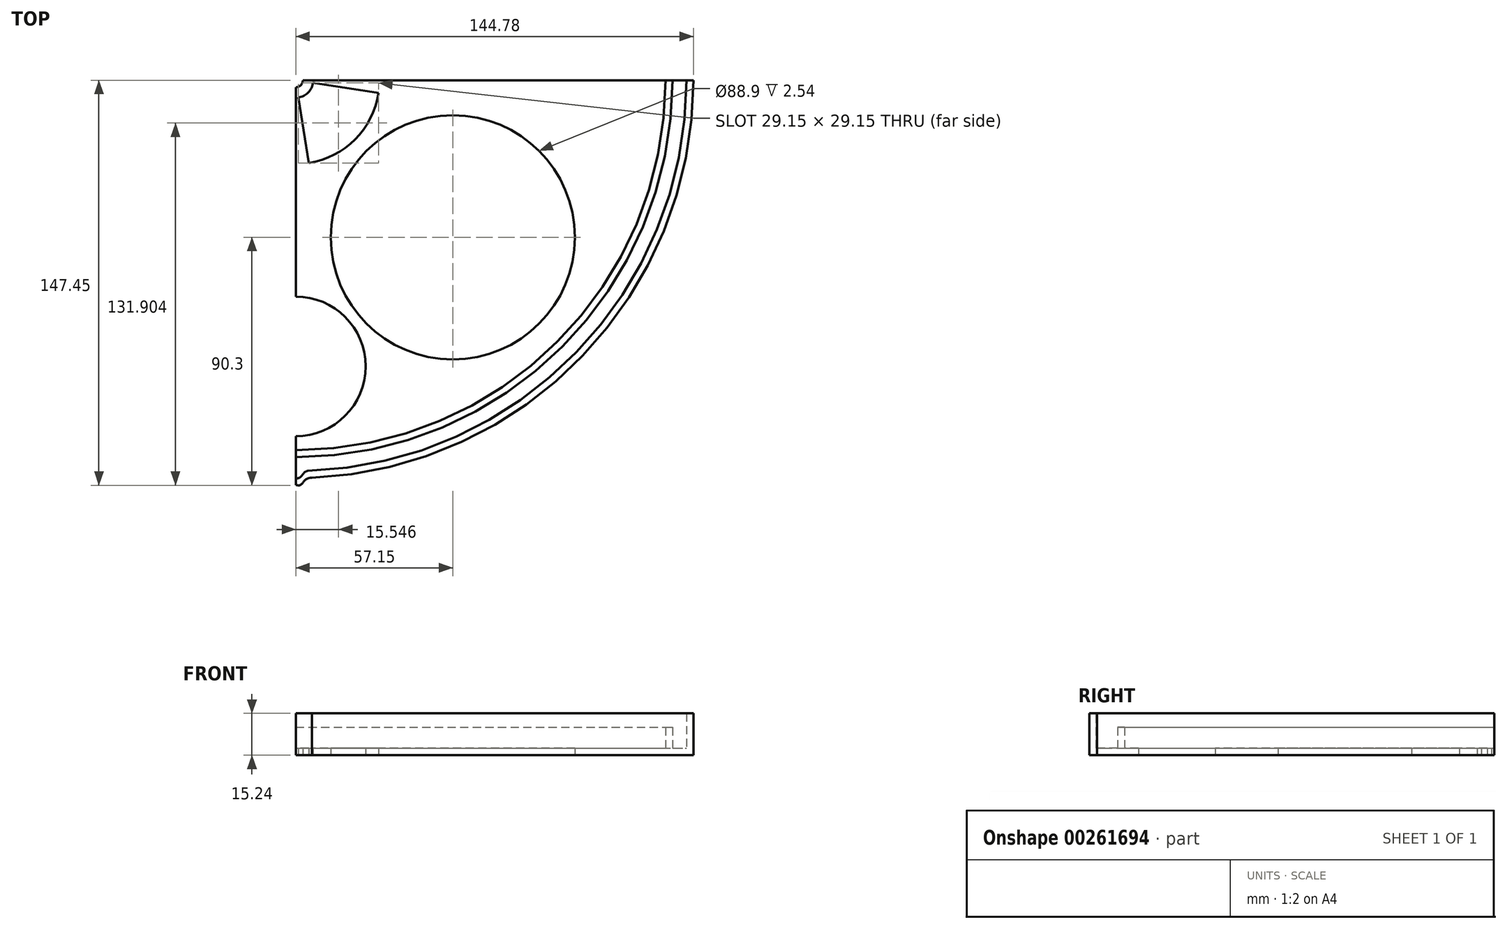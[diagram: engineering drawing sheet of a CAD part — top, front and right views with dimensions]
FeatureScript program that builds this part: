
annotation { "Feature Type Name" : "Feature", "Feature Type Description" : "" }
export const myFeature = defineFeature(function(context is Context, id is Id, definition is map)
    precondition{}
    {
        {
            var Q0;
            Q0=qCreatedBy(makeId("Top.planeOp"),FACE);
            var sketch = newSketch(context, id + "F0", { "sketchPlane" : qUnion([Q0])});
            skCircle(sketch, "E0", {"center": v(0, 0) * mm, "radius": 134.62 * mm});
            skCircle(sketch, "E1.0", {"center": v(0, 0) * mm, "radius": 137.16 * mm});
            skCircle(sketch, "E2.0", {"center": v(0, 0) * mm, "radius": 144.78 * mm});
            skCircle(sketch, "E3.0", {"center": v(0, 0) * mm, "radius": 142.24 * mm});
            skCircle(sketch, "E4.0", {"center": v(0, 0) * mm, "radius": 2.54 * mm});
            skLineSegment(sketch, "E5", {"start": v(0, 0) * mm, "end": v(0, -147.32) * mm});
            skLineSegment(sketch, "E6", {"start": v(-11.57, -144.32) * mm, "end": v(0, -147.32) * mm});
            skFitSpline(sketch, "E7", {"points": [v(0, -147.32) * mm, v(5.92, -144.66) * mm], "startDerivative": vector(10.02, -2.47) * mm, "endDerivative": vector(12.8, 0.33) * mm});
            skLineSegment(sketch, "E8", {"start": v(-8.6, -141.98) * mm, "end": v(0, -144.78) * mm});
            skFitSpline(sketch, "E9", {"points": [v(0, -144.78) * mm, v(4.46, -142.17) * mm], "startDerivative": vector(6.28, -2.02) * mm, "endDerivative": vector(5.88, 0.14) * mm});
            skLineSegment(sketch, "E10", {"start": v(0, 0) * mm, "end": v(-144.78, 0) * mm});
            skLineSegment(sketch, "E11", {"start": v(0, 0) * mm, "end": v(0, 144.78) * mm});
            skLineSegment(sketch, "E12", {"start": v(0, 0) * mm, "end": v(144.78, 0) * mm});
            skLineSegment(sketch, "E13", {"start": v(0, -12.7) * mm, "end": v(-144.22, -12.7) * mm});
            skLineSegment(sketch, "E14", {"start": v(0, -12.7) * mm, "end": v(144.78, -12.7) * mm});
            skLineSegment(sketch, "E15", {"start": v(0, 12.7) * mm, "end": v(-144.22, 12.7) * mm});
            skLineSegment(sketch, "E16", {"start": v(0, 12.7) * mm, "end": v(144.78, 12.7) * mm});
            skLineSegment(sketch, "E17", {"start": v(-12.7, 0) * mm, "end": v(-12.7, 144.22) * mm});
            skLineSegment(sketch, "E18", {"start": v(12.7, 0) * mm, "end": v(12.7, 144.22) * mm});
            skLineSegment(sketch, "E19", {"start": v(-12.7, 0) * mm, "end": v(-12.7, -144.22) * mm});
            skLineSegment(sketch, "E20", {"start": v(12.7, 0) * mm, "end": v(12.7, -144.22) * mm});
            skCircle(sketch, "E21", {"center": v(-57.15, -57.15) * mm, "radius": 44.45 * mm});
            skCircle(sketch, "E22", {"center": v(57.15, -57.15) * mm, "radius": 44.45 * mm});
            skCircle(sketch, "E23", {"center": v(-57.15, 57.15) * mm, "radius": 44.45 * mm});
            skCircle(sketch, "E24", {"center": v(57.15, 57.15) * mm, "radius": 44.45 * mm});
            skCircle(sketch, "E25", {"center": v(-104.14, 0) * mm, "radius": 25.4 * mm});
            skCircle(sketch, "E26", {"center": v(0, 104.14) * mm, "radius": 25.4 * mm});
            skCircle(sketch, "E27", {"center": v(104.14, 0) * mm, "radius": 25.4 * mm});
            skCircle(sketch, "E28", {"center": v(0, -104.14) * mm, "radius": 25.4 * mm});
            skCircle(sketch, "E29", {"center": v(0, 0) * mm, "radius": 30.48 * mm});
            skLineSegment(sketch, "E30", {"start": v(-12.7, -82.14) * mm, "end": v(0, 0) * mm});
            skLineSegment(sketch, "E31", {"start": v(12.7, -82.14) * mm, "end": v(0, 0) * mm});
            skLineSegment(sketch, "E32", {"start": v(82.14, -12.7) * mm, "end": v(0, 0) * mm});
            skLineSegment(sketch, "E33", {"start": v(82.14, 12.7) * mm, "end": v(0, 0) * mm});
            skLineSegment(sketch, "E34", {"start": v(12.7, 82.14) * mm, "end": v(0, 0) * mm});
            skLineSegment(sketch, "E35", {"start": v(-12.7, 82.14) * mm, "end": v(0, 0) * mm});
            skLineSegment(sketch, "E36", {"start": v(-82.14, -12.7) * mm, "end": v(0, 0) * mm});
            skLineSegment(sketch, "E37", {"start": v(-82.14, 12.7) * mm, "end": v(0, 0) * mm});
            skCircle(sketch, "E38", {"center": v(0, 0) * mm, "radius": 6.35 * mm});
            skSolve(sketch);
        }
        {
            var Q0;
            {var subQ1=sQuery(id+"F0.wireOp",EDGE,"E0");var subQ7=sQuery(id+"F0.wireOp",EDGE,"E20");var subQ12=makeQuery(id+"F0.imprint","INTERSECT",VERTEX,{"derivedFrom":[subQ1,subQ7]});Q0=makeQuery(id+"F0.imprint","IMPRINT",FACE,{"disambiguationData":[TD([[makeQuery(id+"F0.imprint","IMPRINT",EDGE,{"disambiguationData":[TD([[subQ12,-1.0]])],"derivedFrom":subQ1}),1.0]])]});}
            var Q1;
            {var subQ0=sQuery(id+"F0.wireOp",EDGE,"E5");var subQ1=sQuery(id+"F0.wireOp",EDGE,"E0");var subQ2=makeQuery(id+"F0.imprint","INTERSECT",VERTEX,{"derivedFrom":[subQ1,subQ0]});Q1=makeQuery(id+"F0.imprint","IMPRINT",FACE,{"disambiguationData":[TD([[makeQuery(id+"F0.imprint","IMPRINT",EDGE,{"disambiguationData":[TD([[subQ2,-1.0]])],"derivedFrom":subQ1}),1.0]])]});}
            var Q2;
            {var subQ0=sQuery(id+"F0.wireOp",EDGE,"E29");var subQ1=sQuery(id+"F0.wireOp",EDGE,"E5");var subQ2=makeQuery(id+"F0.imprint","INTERSECT",VERTEX,{"derivedFrom":[subQ1,subQ0]});Q2=makeQuery(id+"F0.imprint","IMPRINT",FACE,{"disambiguationData":[TD([[makeQuery(id+"F0.imprint","IMPRINT",EDGE,{"disambiguationData":[TD([[subQ2,-1.0]])],"derivedFrom":subQ1}),1.0]])]});}
            var Q3;
            {var subQ0=sQuery(id+"F0.wireOp",EDGE,"E29");var subQ1=sQuery(id+"F0.wireOp",EDGE,"E20");var subQ2=makeQuery(id+"F0.imprint","INTERSECT",VERTEX,{"derivedFrom":[subQ1,subQ0]});Q3=makeQuery(id+"F0.imprint","IMPRINT",FACE,{"disambiguationData":[TD([[makeQuery(id+"F0.imprint","IMPRINT",EDGE,{"disambiguationData":[TD([[subQ2,-1.0]])],"derivedFrom":subQ1}),-1.0]])]});}
            var Q4;
            {var subQ1=sQuery(id+"F0.wireOp",EDGE,"E5");var subQ3=sQuery(id+"F0.wireOp",EDGE,"E29");var subQ4=makeQuery(id+"F0.imprint","INTERSECT",VERTEX,{"derivedFrom":[subQ1,subQ3]});Q4=makeQuery(id+"F0.imprint","IMPRINT",FACE,{"disambiguationData":[TD([[makeQuery(id+"F0.imprint","IMPRINT",EDGE,{"disambiguationData":[TD([[subQ4,-1.0]])],"derivedFrom":subQ3}),1.0]])]});}
            var Q5;
            {var subQ0=sQuery(id+"F0.wireOp",EDGE,"E14");var subQ5=sQuery(id+"F0.wireOp",EDGE,"E31");var subQ6=makeQuery(id+"F0.imprint","INTERSECT",VERTEX,{"derivedFrom":[subQ0,subQ5]});Q5=makeQuery(id+"F0.imprint","IMPRINT",FACE,{"disambiguationData":[TD([[makeQuery(id+"F0.imprint","IMPRINT",EDGE,{"disambiguationData":[TD([[subQ6,-1.0]])],"derivedFrom":subQ5}),1.0]])]});}
            var Q6;
            {var subQ0=sQuery(id+"F0.wireOp",EDGE,"E5");var subQ1=sQuery(id+"F0.wireOp",EDGE,"E4.0");var subQ2=makeQuery(id+"F0.imprint","INTERSECT",VERTEX,{"derivedFrom":[subQ1,subQ0]});Q6=makeQuery(id+"F0.imprint","IMPRINT",FACE,{"disambiguationData":[TD([[makeQuery(id+"F0.imprint","IMPRINT",EDGE,{"disambiguationData":[TD([[subQ2,-1.0]])],"derivedFrom":subQ1}),-1.0]])]});}
            var Q7;
            {var subQ0=sQuery(id+"F0.wireOp",EDGE,"E31");var subQ1=sQuery(id+"F0.wireOp",EDGE,"E4.0");var subQ2=makeQuery(id+"F0.imprint","INTERSECT",VERTEX,{"derivedFrom":[subQ1,subQ0]});Q7=makeQuery(id+"F0.imprint","IMPRINT",FACE,{"disambiguationData":[TD([[makeQuery(id+"F0.imprint","IMPRINT",EDGE,{"disambiguationData":[TD([[subQ2,-1.0]])],"derivedFrom":subQ1}),-1.0]])]});}
            var Q8;
            {var subQ0=sQuery(id+"F0.wireOp",EDGE,"E12");var subQ1=sQuery(id+"F0.wireOp",EDGE,"E4.0");var subQ2=makeQuery(id+"F0.imprint","INTERSECT",VERTEX,{"derivedFrom":[subQ1,subQ0]});Q8=makeQuery(id+"F0.imprint","IMPRINT",FACE,{"disambiguationData":[TD([[makeQuery(id+"F0.imprint","IMPRINT",EDGE,{"disambiguationData":[TD([[subQ2,1.0]])],"derivedFrom":subQ1}),-1.0]])]});}
            var Q9;
            {var subQ0=sQuery(id+"F0.wireOp",EDGE,"E20");var subQ5=sQuery(id+"F0.wireOp",EDGE,"E32");var subQ6=makeQuery(id+"F0.imprint","INTERSECT",VERTEX,{"derivedFrom":[subQ0,subQ5]});Q9=makeQuery(id+"F0.imprint","IMPRINT",FACE,{"disambiguationData":[TD([[makeQuery(id+"F0.imprint","IMPRINT",EDGE,{"disambiguationData":[TD([[subQ6,-1.0]])],"derivedFrom":subQ5}),-1.0]])]});}
            var Q10;
            {var subQ1=sQuery(id+"F0.wireOp",EDGE,"E12");var subQ3=sQuery(id+"F0.wireOp",EDGE,"E29");var subQ4=makeQuery(id+"F0.imprint","INTERSECT",VERTEX,{"derivedFrom":[subQ1,subQ3]});Q10=makeQuery(id+"F0.imprint","IMPRINT",FACE,{"disambiguationData":[TD([[makeQuery(id+"F0.imprint","IMPRINT",EDGE,{"disambiguationData":[TD([[subQ4,1.0]])],"derivedFrom":subQ3}),1.0]])]});}
            var Q11;
            {var subQ0=sQuery(id+"F0.wireOp",EDGE,"E29");var subQ1=sQuery(id+"F0.wireOp",EDGE,"E14");var subQ2=makeQuery(id+"F0.imprint","INTERSECT",VERTEX,{"derivedFrom":[subQ1,subQ0]});Q11=makeQuery(id+"F0.imprint","IMPRINT",FACE,{"disambiguationData":[TD([[makeQuery(id+"F0.imprint","IMPRINT",EDGE,{"disambiguationData":[TD([[subQ2,-1.0]])],"derivedFrom":subQ1}),-1.0]])]});}
            var Q12;
            {var subQ0=sQuery(id+"F0.wireOp",EDGE,"E29");var subQ1=sQuery(id+"F0.wireOp",EDGE,"E14");var subQ2=makeQuery(id+"F0.imprint","INTERSECT",VERTEX,{"derivedFrom":[subQ1,subQ0]});Q12=makeQuery(id+"F0.imprint","IMPRINT",FACE,{"disambiguationData":[TD([[makeQuery(id+"F0.imprint","IMPRINT",EDGE,{"disambiguationData":[TD([[subQ2,-1.0]])],"derivedFrom":subQ1}),1.0]])]});}
            var Q13;
            {var subQ0=sQuery(id+"F0.wireOp",EDGE,"E29");var subQ1=sQuery(id+"F0.wireOp",EDGE,"E12");var subQ2=makeQuery(id+"F0.imprint","INTERSECT",VERTEX,{"derivedFrom":[subQ1,subQ0]});Q13=makeQuery(id+"F0.imprint","IMPRINT",FACE,{"disambiguationData":[TD([[makeQuery(id+"F0.imprint","IMPRINT",EDGE,{"disambiguationData":[TD([[subQ2,-1.0]])],"derivedFrom":subQ1}),-1.0]])]});}
            var Q14;
            {var subQ0=sQuery(id+"F0.wireOp",EDGE,"E12");var subQ1=sQuery(id+"F0.wireOp",EDGE,"E0");var subQ2=makeQuery(id+"F0.imprint","INTERSECT",VERTEX,{"derivedFrom":[subQ1,subQ0]});Q14=makeQuery(id+"F0.imprint","IMPRINT",FACE,{"disambiguationData":[TD([[makeQuery(id+"F0.imprint","IMPRINT",EDGE,{"disambiguationData":[TD([[subQ2,1.0]])],"derivedFrom":subQ1}),1.0]])]});}
            var Q15;
            {var subQ0=sQuery(id+"F0.wireOp",EDGE,"E27");var subQ1=sQuery(id+"F0.wireOp",EDGE,"E14");var subQ3=makeQuery(id+"F0.imprint","INTERSECT",VERTEX,{"derivedFrom":[subQ1,subQ0]});Q15=makeQuery(id+"F0.imprint","IMPRINT",FACE,{"disambiguationData":[TD([[makeQuery(id+"F0.imprint","IMPRINT",EDGE,{"disambiguationData":[TD([[subQ3,1.0]])],"derivedFrom":subQ1}),-1.0]])]});}
            var Q16;
            {var subQ0=sQuery(id+"F0.wireOp",EDGE,"E27");var subQ1=sQuery(id+"F0.wireOp",EDGE,"E12");var subQ2=makeQuery(id+"F0.imprint","INTERSECT",VERTEX,{"disambiguationData":[OD(0.0)],"derivedFrom":[subQ1,subQ0]});Q16=makeQuery(id+"F0.imprint","IMPRINT",FACE,{"disambiguationData":[TD([[makeQuery(id+"F0.imprint","IMPRINT",EDGE,{"disambiguationData":[TD([[subQ2,-1.0]])],"derivedFrom":subQ1}),-1.0]])]});}
            extrude(context, id + "F1", {"entities" : qUnion([Q0, Q1, Q2, Q3, Q4, Q5, Q6, Q7, Q8, Q9, Q10, Q11, Q12, Q13, Q14, Q15, Q16]), "offsetDistance" : 25.4 * mm, "depth" : 2.54 * mm});
        }
        {
            var Q0;
            {var subQ0=sQuery(id+"F0.wireOp",EDGE,"E5");var subQ1=sQuery(id+"F0.wireOp",EDGE,"E0");var subQ2=makeQuery(id+"F0.imprint","INTERSECT",VERTEX,{"derivedFrom":[subQ1,subQ0]});Q0=makeQuery(id+"F0.imprint","IMPRINT",FACE,{"disambiguationData":[TD([[makeQuery(id+"F0.imprint","IMPRINT",EDGE,{"disambiguationData":[TD([[subQ2,-1.0]])],"derivedFrom":subQ1}),-1.0]])]});}
            var Q1;
            {var subQ0=sQuery(id+"F0.wireOp",EDGE,"E20");var subQ1=sQuery(id+"F0.wireOp",EDGE,"E0");var subQ2=makeQuery(id+"F0.imprint","INTERSECT",VERTEX,{"derivedFrom":[subQ1,subQ0]});Q1=makeQuery(id+"F0.imprint","IMPRINT",FACE,{"disambiguationData":[TD([[makeQuery(id+"F0.imprint","IMPRINT",EDGE,{"disambiguationData":[TD([[subQ2,-1.0]])],"derivedFrom":subQ1}),-1.0]])]});}
            var Q2;
            {var subQ0=sQuery(id+"F0.wireOp",EDGE,"E12");var subQ1=sQuery(id+"F0.wireOp",EDGE,"E0");var subQ2=makeQuery(id+"F0.imprint","INTERSECT",VERTEX,{"derivedFrom":[subQ1,subQ0]});Q2=makeQuery(id+"F0.imprint","IMPRINT",FACE,{"disambiguationData":[TD([[makeQuery(id+"F0.imprint","IMPRINT",EDGE,{"disambiguationData":[TD([[subQ2,1.0]])],"derivedFrom":subQ1}),-1.0]])]});}
            extrude(context, id + "F2", {"entities" : qUnion([Q0, Q1, Q2]), "operationType" : NewBodyOperationType.ADD, "offsetDistance" : 25.4 * mm, "depth" : 10.16 * mm});
        }
        {
            var Q0;
            {var subQ0=sQuery(id+"F0.wireOp",EDGE,"E5");var subQ1=sQuery(id+"F0.wireOp",EDGE,"E1.0");var subQ2=makeQuery(id+"F0.imprint","INTERSECT",VERTEX,{"derivedFrom":[subQ1,subQ0]});Q0=makeQuery(id+"F0.imprint","IMPRINT",FACE,{"disambiguationData":[TD([[makeQuery(id+"F0.imprint","IMPRINT",EDGE,{"disambiguationData":[TD([[subQ2,-1.0]])],"derivedFrom":subQ1}),-1.0]])]});}
            var Q1;
            {var subQ0=sQuery(id+"F0.wireOp",EDGE,"E9");var subQ5=sQuery(id+"F0.wireOp",EDGE,"E3.0");var subQ6=makeQuery(id+"F0.imprint","INTERSECT",VERTEX,{"derivedFrom":[subQ5,subQ0]});Q1=makeQuery(id+"F0.imprint","IMPRINT",FACE,{"disambiguationData":[TD([[makeQuery(id+"F0.imprint","IMPRINT",EDGE,{"disambiguationData":[TD([[subQ6,1.0]])],"derivedFrom":subQ5}),-1.0]])]});}
            var Q2;
            {var subQ0=sQuery(id+"F0.wireOp",EDGE,"E9");var subQ1=sQuery(id+"F0.wireOp",EDGE,"E2.0");var subQ3=makeQuery(id+"F0.imprint","INTERSECT",VERTEX,{"derivedFrom":[subQ1,subQ0]});Q2=makeQuery(id+"F0.imprint","IMPRINT",FACE,{"disambiguationData":[TD([[makeQuery(id+"F0.imprint","IMPRINT",EDGE,{"disambiguationData":[TD([[subQ3,1.0]])],"derivedFrom":subQ1}),-1.0]])]});}
            var Q3;
            {var subQ0=sQuery(id+"F0.wireOp",EDGE,"E12");var subQ1=sQuery(id+"F0.wireOp",EDGE,"E1.0");var subQ2=makeQuery(id+"F0.imprint","INTERSECT",VERTEX,{"derivedFrom":[subQ1,subQ0]});Q3=makeQuery(id+"F0.imprint","IMPRINT",FACE,{"disambiguationData":[TD([[makeQuery(id+"F0.imprint","IMPRINT",EDGE,{"disambiguationData":[TD([[subQ2,1.0]])],"derivedFrom":subQ1}),-1.0]])]});}
            var Q4;
            {var subQ0=sQuery(id+"F0.wireOp",EDGE,"E20");var subQ1=sQuery(id+"F0.wireOp",EDGE,"E1.0");var subQ2=makeQuery(id+"F0.imprint","INTERSECT",VERTEX,{"derivedFrom":[subQ1,subQ0]});Q4=makeQuery(id+"F0.imprint","IMPRINT",FACE,{"disambiguationData":[TD([[makeQuery(id+"F0.imprint","IMPRINT",EDGE,{"disambiguationData":[TD([[subQ2,-1.0]])],"derivedFrom":subQ1}),-1.0]])]});}
            extrude(context, id + "F3", {"entities" : qUnion([Q0, Q1, Q2, Q3, Q4]), "operationType" : NewBodyOperationType.ADD, "offsetDistance" : 25.4 * mm, "depth" : 2.54 * mm});
        }
        {
            var Q0;
            {var subQ0=sQuery(id+"F0.wireOp",EDGE,"E12");var subQ1=sQuery(id+"F0.wireOp",EDGE,"E2.0");var subQ2=makeQuery(id+"F0.imprint","INTERSECT",VERTEX,{"derivedFrom":[subQ1,subQ0]});Q0=makeQuery(id+"F0.imprint","IMPRINT",FACE,{"disambiguationData":[TD([[makeQuery(id+"F0.imprint","IMPRINT",EDGE,{"disambiguationData":[TD([[subQ2,1.0]])],"derivedFrom":subQ1}),1.0]])]});}
            var Q1;
            {var subQ0=sQuery(id+"F0.wireOp",EDGE,"E20");var subQ1=sQuery(id+"F0.wireOp",EDGE,"E2.0");var subQ2=makeQuery(id+"F0.imprint","INTERSECT",VERTEX,{"derivedFrom":[subQ1,subQ0]});Q1=makeQuery(id+"F0.imprint","IMPRINT",FACE,{"disambiguationData":[TD([[makeQuery(id+"F0.imprint","IMPRINT",EDGE,{"disambiguationData":[TD([[subQ2,-1.0]])],"derivedFrom":subQ1}),1.0]])]});}
            var Q2;
            {var subQ0=sQuery(id+"F0.wireOp",EDGE,"E7");var subQ1=sQuery(id+"F0.wireOp",EDGE,"E2.0");var subQ3=makeQuery(id+"F0.imprint","INTERSECT",VERTEX,{"disambiguationData":[OD(1.0)],"derivedFrom":[subQ1,subQ0]});Q2=makeQuery(id+"F0.imprint","IMPRINT",FACE,{"disambiguationData":[TD([[makeQuery(id+"F0.imprint","IMPRINT",EDGE,{"disambiguationData":[TD([[subQ3,1.0]])],"derivedFrom":subQ1}),1.0]])]});}
            var Q3;
            {var subQ0=sQuery(id+"F0.wireOp",EDGE,"E7");var subQ1=sQuery(id+"F0.wireOp",EDGE,"E2.0");var subQ2=makeQuery(id+"F0.imprint","INTERSECT",VERTEX,{"disambiguationData":[OD(1.0)],"derivedFrom":[subQ1,subQ0]});Q3=makeQuery(id+"F0.imprint","IMPRINT",FACE,{"disambiguationData":[TD([[makeQuery(id+"F0.imprint","IMPRINT",EDGE,{"disambiguationData":[TD([[subQ2,1.0]])],"derivedFrom":subQ1}),-1.0]])]});}
            extrude(context, id + "F4", {"entities" : qUnion([Q0, Q1, Q2, Q3]), "operationType" : NewBodyOperationType.ADD, "offsetDistance" : 25.4 * mm, "depth" : 15.24 * mm});
        }
    });
